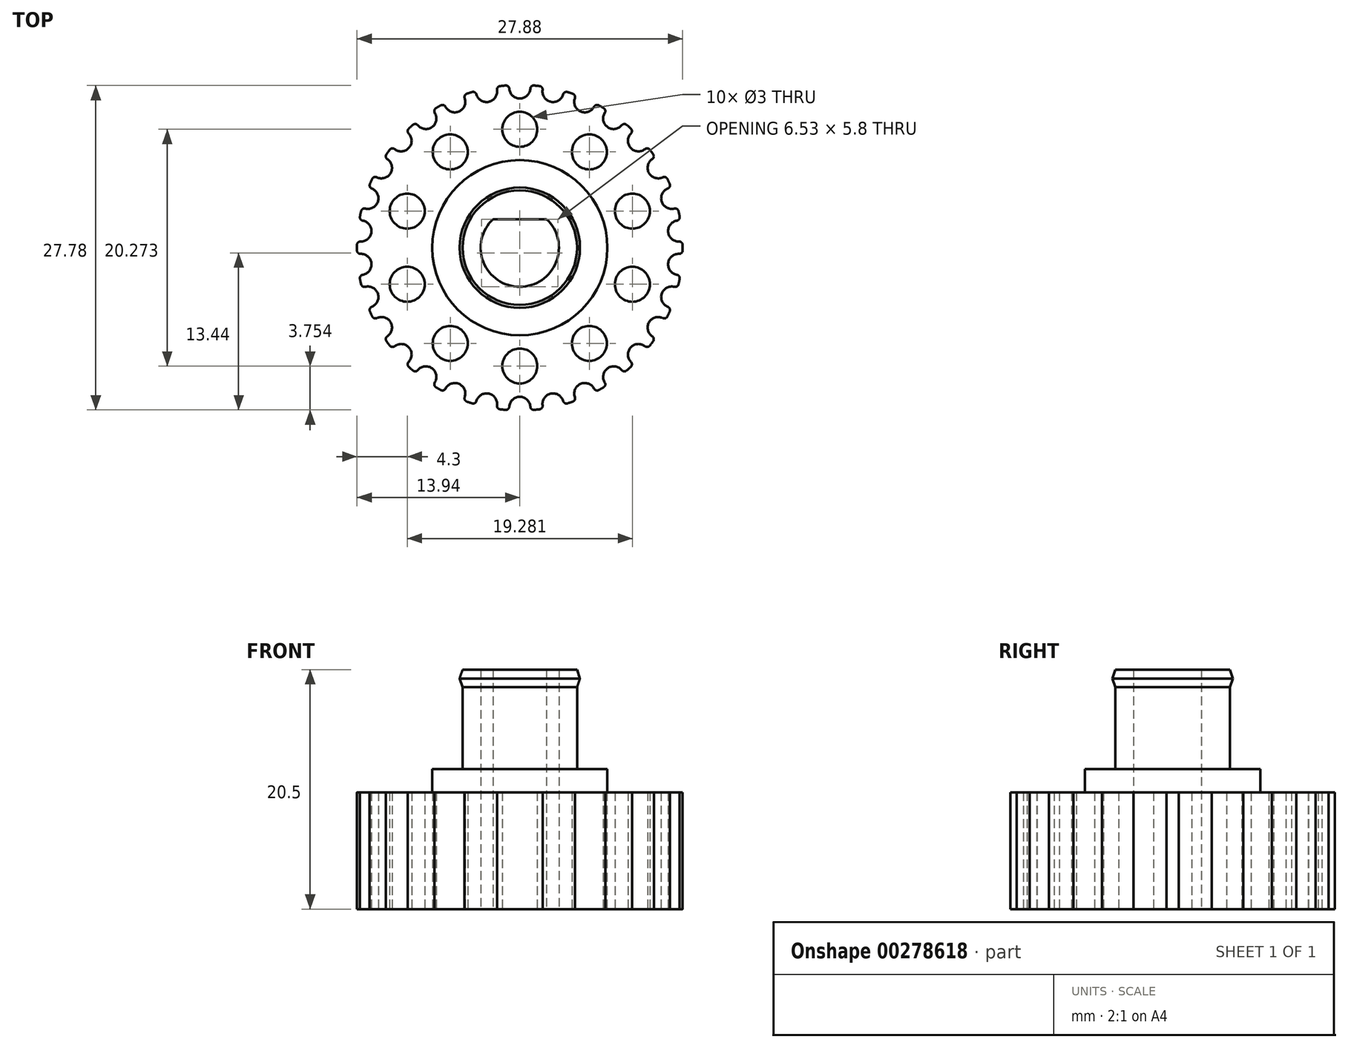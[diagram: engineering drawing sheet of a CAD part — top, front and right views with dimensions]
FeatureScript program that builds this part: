
annotation { "Feature Type Name" : "Feature", "Feature Type Description" : "" }
export const myFeature = defineFeature(function(context is Context, id is Id, definition is map)
    precondition{}
    {
        {
            assignVariable(context, id + "F0", {"name" : "e", "anyValue" : 3});
        }
        {
            assignVariable(context, id + "F1", {"name" : "h1", "anyValue" : 6});
        }
        {
            assignVariable(context, id + "F2", {"name" : "h2", "anyValue" : 6.5 + 5});
        }
        {
            var Q0;
            Q0=qCreatedBy(makeId("Top.planeOp"),FACE);
            var sketch = newSketch(context, id + "F3", { "sketchPlane" : qUnion([Q0])});
            skArc(sketch, "E0", {"start": v(-1.22, 13.89) * mm, "mid": v(0, -13.94) * mm, "end": v(1.22, 13.89) * mm, "construction": true});
            skCircle(sketch, "E1", {"center": v(0, 0) * mm, "radius": 7.5 * mm});
            skCircle(sketch, "E2", {"center": v(0, 0) * mm, "radius": 4.9 * mm});
            skArc(sketch, "E3", {"start": v(-2.28, 2.45) * mm, "mid": v(-3.35, 0) * mm, "end": v(-2.28, -2.45) * mm});
            skLineSegment(sketch, "E4.top", {"start": v(2.28, 2.45) * mm, "end": v(-2.28, 2.45) * mm});
            skArc(sketch, "E5.trimOffspring", {"start": v(2.28, -2.45) * mm, "mid": v(3.35, 0) * mm, "end": v(2.28, 2.45) * mm});
            skPoint(sketch, "E6.orphan", {"position": v(3.35, 2.45) * mm});
            skPoint(sketch, "E7.orphan", {"position": v(3.35, -2.45) * mm});
            skPoint(sketch, "E8.orphan", {"position": v(-3.35, -2.45) * mm});
            skPoint(sketch, "E9.orphan", {"position": v(-3.35, 2.45) * mm});
            skLineSegment(sketch, "E10", {"start": v(0, 7.5) * mm, "end": v(0, 12.77) * mm, "construction": true});
            skCircle(sketch, "E11", {"center": v(0, 0) * mm, "radius": 14.94 * mm});
            skCircle(sketch, "E12", {"center": v(0, 10.14) * mm, "radius": 1.5 * mm});
            skCircle(sketch, "E13.1.0", {"center": v(-5.96, 8.2) * mm, "radius": 1.5 * mm});
            skCircle(sketch, "E13.2.0", {"center": v(-9.64, 3.13) * mm, "radius": 1.5 * mm});
            skCircle(sketch, "E13.3.0", {"center": v(-9.64, -3.13) * mm, "radius": 1.5 * mm});
            skCircle(sketch, "E13.4.0", {"center": v(-5.96, -8.2) * mm, "radius": 1.5 * mm});
            skCircle(sketch, "E13.5.0", {"center": v(0, -10.14) * mm, "radius": 1.5 * mm});
            skCircle(sketch, "E13.6.0", {"center": v(5.96, -8.2) * mm, "radius": 1.5 * mm});
            skCircle(sketch, "E13.7.0", {"center": v(9.64, -3.13) * mm, "radius": 1.5 * mm});
            skCircle(sketch, "E13.8.0", {"center": v(9.64, 3.13) * mm, "radius": 1.5 * mm});
            skCircle(sketch, "E13.9.0", {"center": v(5.96, 8.2) * mm, "radius": 1.5 * mm});
            skCircle(sketch, "E14", {"center": v(0, 0) * mm, "radius": 12.77 * mm, "construction": true});
            skLineSegment(sketch, "E15", {"start": v(0, 12.77) * mm, "end": v(0, 14.94) * mm});
            skArc(sketch, "E16", {"start": v(-0.9, 13.61) * mm, "mid": v(0, 12.77) * mm, "end": v(0.9, 13.61) * mm});
            skArc(sketch, "E17", {"start": v(1.22, 13.89) * mm, "mid": v(1, 13.82) * mm, "end": v(0.9, 13.61) * mm});
            skArc(sketch, "E18.MirrorCS", {"start": v(-1.22, 13.89) * mm, "mid": v(-1, 13.82) * mm, "end": v(-0.9, 13.61) * mm});
            skLineSegment(sketch, "E19", {"start": v(0, 0) * mm, "end": v(1.56, 14.86) * mm, "construction": true});
            skLineSegment(sketch, "E20", {"start": v(0, 0) * mm, "end": v(-1.56, 14.86) * mm, "construction": true});
            skArc(sketch, "E21", {"start": v(1.46, 13.87) * mm, "mid": v(1.34, 13.88) * mm, "end": v(1.22, 13.89) * mm});
            skArc(sketch, "E22.trimOffspring", {"start": v(-1.22, 13.89) * mm, "mid": v(-1.34, 13.88) * mm, "end": v(-1.46, 13.87) * mm});
            skArc(sketch, "E23.1.0", {"start": v(-4.08, 13.33) * mm, "mid": v(-4.2, 13.3) * mm, "end": v(-4.3, 13.26) * mm});
            skArc(sketch, "E23.1.1", {"start": v(-4.08, 13.33) * mm, "mid": v(-3.85, 13.3) * mm, "end": v(-3.7, 13.13) * mm});
            skArc(sketch, "E23.1.2", {"start": v(-3.7, 13.13) * mm, "mid": v(-2.66, 12.5) * mm, "end": v(-1.95, 13.5) * mm});
            skArc(sketch, "E23.1.3", {"start": v(-1.7, 13.84) * mm, "mid": v(-1.9, 13.72) * mm, "end": v(-1.95, 13.5) * mm});
            skArc(sketch, "E23.1.4", {"start": v(-1.46, 13.87) * mm, "mid": v(-1.57, 13.85) * mm, "end": v(-1.7, 13.84) * mm});
            skArc(sketch, "E23.2.0", {"start": v(-6.77, 12.2) * mm, "mid": v(-6.87, 12.13) * mm, "end": v(-6.97, 12.07) * mm});
            skArc(sketch, "E23.2.1", {"start": v(-6.77, 12.2) * mm, "mid": v(-6.54, 12.22) * mm, "end": v(-6.36, 12.07) * mm});
            skArc(sketch, "E23.2.2", {"start": v(-6.36, 12.07) * mm, "mid": v(-5.2, 11.67) * mm, "end": v(-4.72, 12.8) * mm});
            skArc(sketch, "E23.2.3", {"start": v(-4.53, 13.19) * mm, "mid": v(-4.7, 13.03) * mm, "end": v(-4.72, 12.8) * mm});
            skArc(sketch, "E23.2.4", {"start": v(-4.3, 13.26) * mm, "mid": v(-4.42, 13.22) * mm, "end": v(-4.53, 13.19) * mm});
            skArc(sketch, "E23.3.0", {"start": v(-9.15, 10.52) * mm, "mid": v(-9.24, 10.44) * mm, "end": v(-9.33, 10.36) * mm});
            skArc(sketch, "E23.3.1", {"start": v(-9.15, 10.52) * mm, "mid": v(-8.93, 10.6) * mm, "end": v(-8.73, 10.48) * mm});
            skArc(sketch, "E23.3.2", {"start": v(-8.73, 10.48) * mm, "mid": v(-7.5, 10.33) * mm, "end": v(-7.27, 11.54) * mm});
            skArc(sketch, "E23.3.3", {"start": v(-7.17, 11.96) * mm, "mid": v(-7.31, 11.77) * mm, "end": v(-7.27, 11.54) * mm});
            skArc(sketch, "E23.3.4", {"start": v(-6.97, 12.07) * mm, "mid": v(-7.07, 12.02) * mm, "end": v(-7.17, 11.96) * mm});
            skArc(sketch, "E23.4.0", {"start": v(-11.14, 8.38) * mm, "mid": v(-11.21, 8.3) * mm, "end": v(-11.28, 8.2) * mm});
            skArc(sketch, "E23.4.1", {"start": v(-11.14, 8.38) * mm, "mid": v(-10.94, 8.5) * mm, "end": v(-10.72, 8.44) * mm});
            skArc(sketch, "E23.4.2", {"start": v(-10.72, 8.44) * mm, "mid": v(-9.5, 8.55) * mm, "end": v(-9.51, 9.77) * mm});
            skArc(sketch, "E23.4.3", {"start": v(-9.5, 10.2) * mm, "mid": v(-9.6, 10) * mm, "end": v(-9.51, 9.77) * mm});
            skArc(sketch, "E23.4.4", {"start": v(-9.33, 10.36) * mm, "mid": v(-9.42, 10.28) * mm, "end": v(-9.5, 10.2) * mm});
            skArc(sketch, "E23.5.0", {"start": v(-12.64, 5.89) * mm, "mid": v(-12.69, 5.78) * mm, "end": v(-12.74, 5.67) * mm});
            skArc(sketch, "E23.5.1", {"start": v(-12.64, 5.89) * mm, "mid": v(-12.47, 6.04) * mm, "end": v(-12.24, 6.03) * mm});
            skArc(sketch, "E23.5.2", {"start": v(-12.24, 6.03) * mm, "mid": v(-11.06, 6.39) * mm, "end": v(-11.34, 7.58) * mm});
            skArc(sketch, "E23.5.3", {"start": v(-11.42, 8) * mm, "mid": v(-11.47, 7.78) * mm, "end": v(-11.34, 7.58) * mm});
            skArc(sketch, "E23.5.4", {"start": v(-11.28, 8.2) * mm, "mid": v(-11.35, 8.1) * mm, "end": v(-11.42, 8) * mm});
            skArc(sketch, "E23.6.0", {"start": v(-13.59, 3.13) * mm, "mid": v(-13.61, 3.01) * mm, "end": v(-13.64, 2.9) * mm});
            skArc(sketch, "E23.6.1", {"start": v(-13.59, 3.13) * mm, "mid": v(-13.45, 3.32) * mm, "end": v(-13.22, 3.35) * mm});
            skArc(sketch, "E23.6.2", {"start": v(-13.22, 3.35) * mm, "mid": v(-12.15, 3.95) * mm, "end": v(-12.67, 5.06) * mm});
            skArc(sketch, "E23.6.3", {"start": v(-12.83, 5.46) * mm, "mid": v(-12.83, 5.22) * mm, "end": v(-12.67, 5.06) * mm});
            skArc(sketch, "E23.6.4", {"start": v(-12.74, 5.67) * mm, "mid": v(-12.78, 5.56) * mm, "end": v(-12.83, 5.46) * mm});
            skArc(sketch, "E23.7.0", {"start": v(-13.94, 0.24) * mm, "mid": v(-13.94, 0.12) * mm, "end": v(-13.94, 0) * mm});
            skArc(sketch, "E23.7.1", {"start": v(-13.94, 0.24) * mm, "mid": v(-13.85, 0.45) * mm, "end": v(-13.63, 0.53) * mm});
            skArc(sketch, "E23.7.2", {"start": v(-13.63, 0.53) * mm, "mid": v(-12.7, 1.34) * mm, "end": v(-13.44, 2.32) * mm});
            skArc(sketch, "E23.7.3", {"start": v(-13.69, 2.67) * mm, "mid": v(-13.64, 2.44) * mm, "end": v(-13.44, 2.32) * mm});
            skArc(sketch, "E23.7.4", {"start": v(-13.64, 2.9) * mm, "mid": v(-13.66, 2.78) * mm, "end": v(-13.69, 2.67) * mm});
            skArc(sketch, "E23.8.0", {"start": v(-13.69, -2.67) * mm, "mid": v(-13.66, -2.78) * mm, "end": v(-13.64, -2.9) * mm});
            skArc(sketch, "E23.8.1", {"start": v(-13.69, -2.67) * mm, "mid": v(-13.64, -2.44) * mm, "end": v(-13.44, -2.32) * mm});
            skArc(sketch, "E23.8.2", {"start": v(-13.44, -2.32) * mm, "mid": v(-12.7, -1.34) * mm, "end": v(-13.63, -0.53) * mm});
            skArc(sketch, "E23.8.3", {"start": v(-13.94, -0.24) * mm, "mid": v(-13.85, -0.45) * mm, "end": v(-13.63, -0.53) * mm});
            skArc(sketch, "E23.8.4", {"start": v(-13.94, 0) * mm, "mid": v(-13.94, -0.12) * mm, "end": v(-13.94, -0.24) * mm});
            skArc(sketch, "E23.9.0", {"start": v(-12.83, -5.46) * mm, "mid": v(-12.78, -5.56) * mm, "end": v(-12.74, -5.67) * mm});
            skArc(sketch, "E23.9.1", {"start": v(-12.83, -5.46) * mm, "mid": v(-12.83, -5.22) * mm, "end": v(-12.67, -5.06) * mm});
            skArc(sketch, "E23.9.2", {"start": v(-12.67, -5.06) * mm, "mid": v(-12.15, -3.95) * mm, "end": v(-13.22, -3.35) * mm});
            skArc(sketch, "E23.9.3", {"start": v(-13.59, -3.13) * mm, "mid": v(-13.45, -3.32) * mm, "end": v(-13.22, -3.35) * mm});
            skArc(sketch, "E23.9.4", {"start": v(-13.64, -2.9) * mm, "mid": v(-13.61, -3.01) * mm, "end": v(-13.59, -3.13) * mm});
            skArc(sketch, "E23.10.0", {"start": v(-11.42, -8) * mm, "mid": v(-11.35, -8.1) * mm, "end": v(-11.28, -8.2) * mm});
            skArc(sketch, "E23.10.1", {"start": v(-11.42, -8) * mm, "mid": v(-11.47, -7.78) * mm, "end": v(-11.34, -7.58) * mm});
            skArc(sketch, "E23.10.2", {"start": v(-11.34, -7.58) * mm, "mid": v(-11.06, -6.39) * mm, "end": v(-12.24, -6.03) * mm});
            skArc(sketch, "E23.10.3", {"start": v(-12.64, -5.89) * mm, "mid": v(-12.47, -6.04) * mm, "end": v(-12.24, -6.03) * mm});
            skArc(sketch, "E23.10.4", {"start": v(-12.74, -5.67) * mm, "mid": v(-12.69, -5.78) * mm, "end": v(-12.64, -5.89) * mm});
            skArc(sketch, "E23.11.0", {"start": v(-9.5, -10.2) * mm, "mid": v(-9.42, -10.28) * mm, "end": v(-9.33, -10.36) * mm});
            skArc(sketch, "E23.11.1", {"start": v(-9.5, -10.2) * mm, "mid": v(-9.6, -10) * mm, "end": v(-9.51, -9.77) * mm});
            skArc(sketch, "E23.11.2", {"start": v(-9.51, -9.77) * mm, "mid": v(-9.5, -8.55) * mm, "end": v(-10.72, -8.44) * mm});
            skArc(sketch, "E23.11.3", {"start": v(-11.14, -8.38) * mm, "mid": v(-10.94, -8.5) * mm, "end": v(-10.72, -8.44) * mm});
            skArc(sketch, "E23.11.4", {"start": v(-11.28, -8.2) * mm, "mid": v(-11.21, -8.3) * mm, "end": v(-11.14, -8.38) * mm});
            skArc(sketch, "E23.12.0", {"start": v(-7.17, -11.96) * mm, "mid": v(-7.07, -12.02) * mm, "end": v(-6.97, -12.07) * mm});
            skArc(sketch, "E23.12.1", {"start": v(-7.17, -11.96) * mm, "mid": v(-7.31, -11.77) * mm, "end": v(-7.27, -11.54) * mm});
            skArc(sketch, "E23.12.2", {"start": v(-7.27, -11.54) * mm, "mid": v(-7.5, -10.33) * mm, "end": v(-8.73, -10.48) * mm});
            skArc(sketch, "E23.12.3", {"start": v(-9.15, -10.52) * mm, "mid": v(-8.93, -10.6) * mm, "end": v(-8.73, -10.48) * mm});
            skArc(sketch, "E23.12.4", {"start": v(-9.33, -10.36) * mm, "mid": v(-9.24, -10.44) * mm, "end": v(-9.15, -10.52) * mm});
            skArc(sketch, "E23.13.0", {"start": v(-4.53, -13.19) * mm, "mid": v(-4.42, -13.22) * mm, "end": v(-4.3, -13.26) * mm});
            skArc(sketch, "E23.13.1", {"start": v(-4.53, -13.19) * mm, "mid": v(-4.7, -13.03) * mm, "end": v(-4.72, -12.8) * mm});
            skArc(sketch, "E23.13.2", {"start": v(-4.72, -12.8) * mm, "mid": v(-5.2, -11.67) * mm, "end": v(-6.36, -12.07) * mm});
            skArc(sketch, "E23.13.3", {"start": v(-6.77, -12.2) * mm, "mid": v(-6.54, -12.22) * mm, "end": v(-6.36, -12.07) * mm});
            skArc(sketch, "E23.13.4", {"start": v(-6.97, -12.07) * mm, "mid": v(-6.87, -12.13) * mm, "end": v(-6.77, -12.2) * mm});
            skArc(sketch, "E23.14.0", {"start": v(-1.7, -13.84) * mm, "mid": v(-1.57, -13.85) * mm, "end": v(-1.46, -13.87) * mm});
            skArc(sketch, "E23.14.1", {"start": v(-1.7, -13.84) * mm, "mid": v(-1.9, -13.72) * mm, "end": v(-1.95, -13.5) * mm});
            skArc(sketch, "E23.14.2", {"start": v(-1.95, -13.5) * mm, "mid": v(-2.66, -12.5) * mm, "end": v(-3.7, -13.13) * mm});
            skArc(sketch, "E23.14.3", {"start": v(-4.08, -13.33) * mm, "mid": v(-3.85, -13.3) * mm, "end": v(-3.7, -13.13) * mm});
            skArc(sketch, "E23.14.4", {"start": v(-4.3, -13.26) * mm, "mid": v(-4.2, -13.3) * mm, "end": v(-4.08, -13.33) * mm});
            skArc(sketch, "E23.15.0", {"start": v(1.22, -13.89) * mm, "mid": v(1.34, -13.88) * mm, "end": v(1.46, -13.87) * mm});
            skArc(sketch, "E23.15.1", {"start": v(1.22, -13.89) * mm, "mid": v(1, -13.82) * mm, "end": v(0.9, -13.61) * mm});
            skArc(sketch, "E23.15.2", {"start": v(0.9, -13.61) * mm, "mid": v(0, -12.77) * mm, "end": v(-0.9, -13.61) * mm});
            skArc(sketch, "E23.15.3", {"start": v(-1.22, -13.89) * mm, "mid": v(-1, -13.82) * mm, "end": v(-0.9, -13.61) * mm});
            skArc(sketch, "E23.15.4", {"start": v(-1.46, -13.87) * mm, "mid": v(-1.34, -13.88) * mm, "end": v(-1.22, -13.89) * mm});
            skArc(sketch, "E23.16.0", {"start": v(4.08, -13.33) * mm, "mid": v(4.2, -13.3) * mm, "end": v(4.3, -13.26) * mm});
            skArc(sketch, "E23.16.1", {"start": v(4.08, -13.33) * mm, "mid": v(3.85, -13.3) * mm, "end": v(3.7, -13.13) * mm});
            skArc(sketch, "E23.16.2", {"start": v(3.7, -13.13) * mm, "mid": v(2.66, -12.5) * mm, "end": v(1.95, -13.5) * mm});
            skArc(sketch, "E23.16.3", {"start": v(1.7, -13.84) * mm, "mid": v(1.9, -13.72) * mm, "end": v(1.95, -13.5) * mm});
            skArc(sketch, "E23.16.4", {"start": v(1.46, -13.87) * mm, "mid": v(1.57, -13.85) * mm, "end": v(1.7, -13.84) * mm});
            skArc(sketch, "E23.17.0", {"start": v(6.77, -12.2) * mm, "mid": v(6.87, -12.13) * mm, "end": v(6.97, -12.07) * mm});
            skArc(sketch, "E23.17.1", {"start": v(6.77, -12.2) * mm, "mid": v(6.54, -12.22) * mm, "end": v(6.36, -12.07) * mm});
            skArc(sketch, "E23.17.2", {"start": v(6.36, -12.07) * mm, "mid": v(5.2, -11.67) * mm, "end": v(4.72, -12.8) * mm});
            skArc(sketch, "E23.17.3", {"start": v(4.53, -13.19) * mm, "mid": v(4.7, -13.03) * mm, "end": v(4.72, -12.8) * mm});
            skArc(sketch, "E23.17.4", {"start": v(4.3, -13.26) * mm, "mid": v(4.42, -13.22) * mm, "end": v(4.53, -13.19) * mm});
            skArc(sketch, "E23.18.0", {"start": v(9.15, -10.52) * mm, "mid": v(9.24, -10.44) * mm, "end": v(9.33, -10.36) * mm});
            skArc(sketch, "E23.18.1", {"start": v(9.15, -10.52) * mm, "mid": v(8.93, -10.6) * mm, "end": v(8.73, -10.48) * mm});
            skArc(sketch, "E23.18.2", {"start": v(8.73, -10.48) * mm, "mid": v(7.5, -10.33) * mm, "end": v(7.27, -11.54) * mm});
            skArc(sketch, "E23.18.3", {"start": v(7.17, -11.96) * mm, "mid": v(7.31, -11.77) * mm, "end": v(7.27, -11.54) * mm});
            skArc(sketch, "E23.18.4", {"start": v(6.97, -12.07) * mm, "mid": v(7.07, -12.02) * mm, "end": v(7.17, -11.96) * mm});
            skArc(sketch, "E23.19.0", {"start": v(11.14, -8.38) * mm, "mid": v(11.21, -8.3) * mm, "end": v(11.28, -8.2) * mm});
            skArc(sketch, "E23.19.1", {"start": v(11.14, -8.38) * mm, "mid": v(10.94, -8.5) * mm, "end": v(10.72, -8.44) * mm});
            skArc(sketch, "E23.19.2", {"start": v(10.72, -8.44) * mm, "mid": v(9.5, -8.55) * mm, "end": v(9.51, -9.77) * mm});
            skArc(sketch, "E23.19.3", {"start": v(9.5, -10.2) * mm, "mid": v(9.6, -10) * mm, "end": v(9.51, -9.77) * mm});
            skArc(sketch, "E23.19.4", {"start": v(9.33, -10.36) * mm, "mid": v(9.42, -10.28) * mm, "end": v(9.5, -10.2) * mm});
            skArc(sketch, "E23.20.0", {"start": v(12.64, -5.89) * mm, "mid": v(12.69, -5.78) * mm, "end": v(12.74, -5.67) * mm});
            skArc(sketch, "E23.20.1", {"start": v(12.64, -5.89) * mm, "mid": v(12.47, -6.04) * mm, "end": v(12.24, -6.03) * mm});
            skArc(sketch, "E23.20.2", {"start": v(12.24, -6.03) * mm, "mid": v(11.06, -6.39) * mm, "end": v(11.34, -7.58) * mm});
            skArc(sketch, "E23.20.3", {"start": v(11.42, -8) * mm, "mid": v(11.47, -7.78) * mm, "end": v(11.34, -7.58) * mm});
            skArc(sketch, "E23.20.4", {"start": v(11.28, -8.2) * mm, "mid": v(11.35, -8.1) * mm, "end": v(11.42, -8) * mm});
            skArc(sketch, "E23.21.0", {"start": v(13.59, -3.13) * mm, "mid": v(13.61, -3.01) * mm, "end": v(13.64, -2.9) * mm});
            skArc(sketch, "E23.21.1", {"start": v(13.59, -3.13) * mm, "mid": v(13.45, -3.32) * mm, "end": v(13.22, -3.35) * mm});
            skArc(sketch, "E23.21.2", {"start": v(13.22, -3.35) * mm, "mid": v(12.15, -3.95) * mm, "end": v(12.67, -5.06) * mm});
            skArc(sketch, "E23.21.3", {"start": v(12.83, -5.46) * mm, "mid": v(12.83, -5.22) * mm, "end": v(12.67, -5.06) * mm});
            skArc(sketch, "E23.21.4", {"start": v(12.74, -5.67) * mm, "mid": v(12.78, -5.56) * mm, "end": v(12.83, -5.46) * mm});
            skArc(sketch, "E23.22.0", {"start": v(13.94, -0.24) * mm, "mid": v(13.94, -0.12) * mm, "end": v(13.94, 0) * mm});
            skArc(sketch, "E23.22.1", {"start": v(13.94, -0.24) * mm, "mid": v(13.85, -0.45) * mm, "end": v(13.63, -0.53) * mm});
            skArc(sketch, "E23.22.2", {"start": v(13.63, -0.53) * mm, "mid": v(12.7, -1.34) * mm, "end": v(13.44, -2.32) * mm});
            skArc(sketch, "E23.22.3", {"start": v(13.69, -2.67) * mm, "mid": v(13.64, -2.44) * mm, "end": v(13.44, -2.32) * mm});
            skArc(sketch, "E23.22.4", {"start": v(13.64, -2.9) * mm, "mid": v(13.66, -2.78) * mm, "end": v(13.69, -2.67) * mm});
            skArc(sketch, "E23.23.0", {"start": v(13.69, 2.67) * mm, "mid": v(13.66, 2.78) * mm, "end": v(13.64, 2.9) * mm});
            skArc(sketch, "E23.23.1", {"start": v(13.69, 2.67) * mm, "mid": v(13.64, 2.44) * mm, "end": v(13.44, 2.32) * mm});
            skArc(sketch, "E23.23.2", {"start": v(13.44, 2.32) * mm, "mid": v(12.7, 1.34) * mm, "end": v(13.63, 0.53) * mm});
            skArc(sketch, "E23.23.3", {"start": v(13.94, 0.24) * mm, "mid": v(13.85, 0.45) * mm, "end": v(13.63, 0.53) * mm});
            skArc(sketch, "E23.23.4", {"start": v(13.94, 0) * mm, "mid": v(13.94, 0.12) * mm, "end": v(13.94, 0.24) * mm});
            skArc(sketch, "E23.24.0", {"start": v(12.83, 5.46) * mm, "mid": v(12.78, 5.56) * mm, "end": v(12.74, 5.67) * mm});
            skArc(sketch, "E23.24.1", {"start": v(12.83, 5.46) * mm, "mid": v(12.83, 5.22) * mm, "end": v(12.67, 5.06) * mm});
            skArc(sketch, "E23.24.2", {"start": v(12.67, 5.06) * mm, "mid": v(12.15, 3.95) * mm, "end": v(13.22, 3.35) * mm});
            skArc(sketch, "E23.24.3", {"start": v(13.59, 3.13) * mm, "mid": v(13.45, 3.32) * mm, "end": v(13.22, 3.35) * mm});
            skArc(sketch, "E23.24.4", {"start": v(13.64, 2.9) * mm, "mid": v(13.61, 3.01) * mm, "end": v(13.59, 3.13) * mm});
            skArc(sketch, "E23.25.0", {"start": v(11.42, 8) * mm, "mid": v(11.35, 8.1) * mm, "end": v(11.28, 8.2) * mm});
            skArc(sketch, "E23.25.1", {"start": v(11.42, 8) * mm, "mid": v(11.47, 7.78) * mm, "end": v(11.34, 7.58) * mm});
            skArc(sketch, "E23.25.2", {"start": v(11.34, 7.58) * mm, "mid": v(11.06, 6.39) * mm, "end": v(12.24, 6.03) * mm});
            skArc(sketch, "E23.25.3", {"start": v(12.64, 5.89) * mm, "mid": v(12.47, 6.04) * mm, "end": v(12.24, 6.03) * mm});
            skArc(sketch, "E23.25.4", {"start": v(12.74, 5.67) * mm, "mid": v(12.69, 5.78) * mm, "end": v(12.64, 5.89) * mm});
            skArc(sketch, "E23.26.0", {"start": v(9.5, 10.2) * mm, "mid": v(9.42, 10.28) * mm, "end": v(9.33, 10.36) * mm});
            skArc(sketch, "E23.26.1", {"start": v(9.5, 10.2) * mm, "mid": v(9.6, 10) * mm, "end": v(9.51, 9.77) * mm});
            skArc(sketch, "E23.26.2", {"start": v(9.51, 9.77) * mm, "mid": v(9.5, 8.55) * mm, "end": v(10.72, 8.44) * mm});
            skArc(sketch, "E23.26.3", {"start": v(11.14, 8.38) * mm, "mid": v(10.94, 8.5) * mm, "end": v(10.72, 8.44) * mm});
            skArc(sketch, "E23.26.4", {"start": v(11.28, 8.2) * mm, "mid": v(11.21, 8.3) * mm, "end": v(11.14, 8.38) * mm});
            skArc(sketch, "E23.27.0", {"start": v(7.17, 11.96) * mm, "mid": v(7.07, 12.02) * mm, "end": v(6.97, 12.07) * mm});
            skArc(sketch, "E23.27.1", {"start": v(7.17, 11.96) * mm, "mid": v(7.31, 11.77) * mm, "end": v(7.27, 11.54) * mm});
            skArc(sketch, "E23.27.2", {"start": v(7.27, 11.54) * mm, "mid": v(7.5, 10.33) * mm, "end": v(8.73, 10.48) * mm});
            skArc(sketch, "E23.27.3", {"start": v(9.15, 10.52) * mm, "mid": v(8.93, 10.6) * mm, "end": v(8.73, 10.48) * mm});
            skArc(sketch, "E23.27.4", {"start": v(9.33, 10.36) * mm, "mid": v(9.24, 10.44) * mm, "end": v(9.15, 10.52) * mm});
            skArc(sketch, "E23.28.0", {"start": v(4.53, 13.19) * mm, "mid": v(4.42, 13.22) * mm, "end": v(4.3, 13.26) * mm});
            skArc(sketch, "E23.28.1", {"start": v(4.53, 13.19) * mm, "mid": v(4.7, 13.03) * mm, "end": v(4.72, 12.8) * mm});
            skArc(sketch, "E23.28.2", {"start": v(4.72, 12.8) * mm, "mid": v(5.2, 11.67) * mm, "end": v(6.36, 12.07) * mm});
            skArc(sketch, "E23.28.3", {"start": v(6.77, 12.2) * mm, "mid": v(6.54, 12.22) * mm, "end": v(6.36, 12.07) * mm});
            skArc(sketch, "E23.28.4", {"start": v(6.97, 12.07) * mm, "mid": v(6.87, 12.13) * mm, "end": v(6.77, 12.2) * mm});
            skArc(sketch, "E23.29.0", {"start": v(1.7, 13.84) * mm, "mid": v(1.57, 13.85) * mm, "end": v(1.46, 13.87) * mm});
            skArc(sketch, "E23.29.1", {"start": v(1.7, 13.84) * mm, "mid": v(1.9, 13.72) * mm, "end": v(1.95, 13.5) * mm});
            skArc(sketch, "E23.29.2", {"start": v(1.95, 13.5) * mm, "mid": v(2.66, 12.5) * mm, "end": v(3.7, 13.13) * mm});
            skArc(sketch, "E23.29.3", {"start": v(4.08, 13.33) * mm, "mid": v(3.85, 13.3) * mm, "end": v(3.7, 13.13) * mm});
            skArc(sketch, "E23.29.4", {"start": v(4.3, 13.26) * mm, "mid": v(4.2, 13.3) * mm, "end": v(4.08, 13.33) * mm});
            skArc(sketch, "E24", {"start": v(2.28, -2.45) * mm, "mid": v(0, -3.35) * mm, "end": v(-2.28, -2.45) * mm});
            skSolve(sketch);
        }
        {
            var Q0;
            Q0=makeQuery(id+"F3.imprint","IMPRINT",FACE,{"disambiguationData":[TD([[makeQuery(id+"F3.imprint","IMPRINT",EDGE,{"derivedFrom":sQuery(id+"F3.wireOp",EDGE,"E1")}),-1.0]])]});
            var Q1;
            Q1=makeQuery(id+"F3.imprint","IMPRINT",FACE,{"disambiguationData":[TD([[makeQuery(id+"F3.imprint","IMPRINT",EDGE,{"derivedFrom":sQuery(id+"F3.wireOp",EDGE,"E1")}),1.0]])]});
            var Q2;
            Q2=makeQuery(id+"F3.imprint","IMPRINT",FACE,{"disambiguationData":[TD([[makeQuery(id+"F3.imprint","IMPRINT",EDGE,{"derivedFrom":sQuery(id+"F3.wireOp",EDGE,"E2")}),1.0]])]});
            extrude(context, id + "F4", {"entities" : qUnion([Q0, Q1, Q2]), "depth" : 10 * mm});
        }
        {
            var Q0;
            Q0=makeQuery(id+"F3.imprint","IMPRINT",FACE,{"disambiguationData":[TD([[makeQuery(id+"F3.imprint","IMPRINT",EDGE,{"derivedFrom":sQuery(id+"F3.wireOp",EDGE,"E1")}),1.0]])]});
            var Q1;
            Q1=makeQuery(id+"F3.imprint","IMPRINT",FACE,{"disambiguationData":[TD([[makeQuery(id+"F3.imprint","IMPRINT",EDGE,{"derivedFrom":sQuery(id+"F3.wireOp",EDGE,"E2")}),1.0]])]});
            extrude(context, id + "F5", {"entities" : qUnion([Q0, Q1]), "depth" : 12 * mm});
        }
        {
            var Q0;
            Q0=makeQuery(id+"F3.imprint","IMPRINT",FACE,{"disambiguationData":[TD([[makeQuery(id+"F3.imprint","IMPRINT",EDGE,{"derivedFrom":sQuery(id+"F3.wireOp",EDGE,"E2")}),1.0]])]});
            extrude(context, id + "F6", {"entities" : qUnion([Q0]), "operationType" : NewBodyOperationType.ADD, "depth" : (getVariable(context, 'e') + getVariable(context, 'h1') + getVariable(context, 'h2')) * mm});
        }
        {
            var Q0;
            Q0=qCreatedBy(makeId("Front.planeOp"),FACE);
            var sketch = newSketch(context, id + "F7", { "sketchPlane" : qUnion([Q0])});
            skLineSegment(sketch, "E25", {"start": v(0, 0) * mm, "end": v(0, 17.5) * mm, "construction": true});
            skLineSegment(sketch, "E26", {"start": v(-4.9, 6) * mm, "end": v(-4.9, 12.5) * mm});
            skLineSegment(sketch, "E27", {"start": v(4.9, 20.5) * mm, "end": v(4.9, 6) * mm});
            skLineSegment(sketch, "E28.bottom", {"start": v(4.9, 20.5) * mm, "end": v(5.15, 20.5) * mm, "construction": true});
            skLineSegment(sketch, "E28.top", {"start": v(4.9, 19) * mm, "end": v(5.15, 19) * mm, "construction": true});
            skLineSegment(sketch, "E28.left", {"start": v(4.9, 20.5) * mm, "end": v(4.9, 19) * mm, "construction": true});
            skLineSegment(sketch, "E28.right", {"start": v(5.15, 20.5) * mm, "end": v(5.15, 19) * mm, "construction": true});
            skPoint(sketch, "E29", {"position": v(5.15, 19.75) * mm});
            skLineSegment(sketch, "E30", {"start": v(4.9, 20.5) * mm, "end": v(5.15, 19.75) * mm});
            skLineSegment(sketch, "E31", {"start": v(5.15, 19.75) * mm, "end": v(4.9, 19) * mm});
            skLineSegment(sketch, "E32", {"start": v(4.9, 19) * mm, "end": v(4.9, 20.5) * mm});
            skSolve(sketch);
        }
        {
            var Q0;
            Q0=makeQuery(id+"F7.imprint","IMPRINT",FACE,{"disambiguationData":[TD([[makeQuery(id+"F7.imprint","IMPRINT",EDGE,{"derivedFrom":sQuery(id+"F7.wireOp",EDGE,"E30")}),-1.0]])]});
            var Q1;
            Q1=sQuery(id+"F7.wireOp",EDGE,"E25");
            revolve(context, id + "F8", {"operationType" : NewBodyOperationType.ADD, "entities" : qUnion([Q0]), "axis" : qUnion([Q1]), "revolveType" : RevolveType.FULL});
        }
        {
            var Q0;
            Q0=makeQuery(id+"F6.opExtrude","CAP_FACE",FACE,{"disambiguationData":[OSD([sQuery(id+"F3.wireOp",EDGE,"E2"),sQuery(id+"F3.wireOp",EDGE,"E3"),sQuery(id+"F3.wireOp",EDGE,"E4.bottom"),sQuery(id+"F3.wireOp",EDGE,"E4.top"),sQuery(id+"F3.wireOp",EDGE,"E5.trimOffspring")])],"isStart":false});
            cPlane(context, id + "F9", {"entities" : qUnion([Q0]), "cplaneType" : CPlaneType.OFFSET, "offset" : 0 * mm, "width" : 150 * mm, "height" : 150 * mm});
        }
    });
